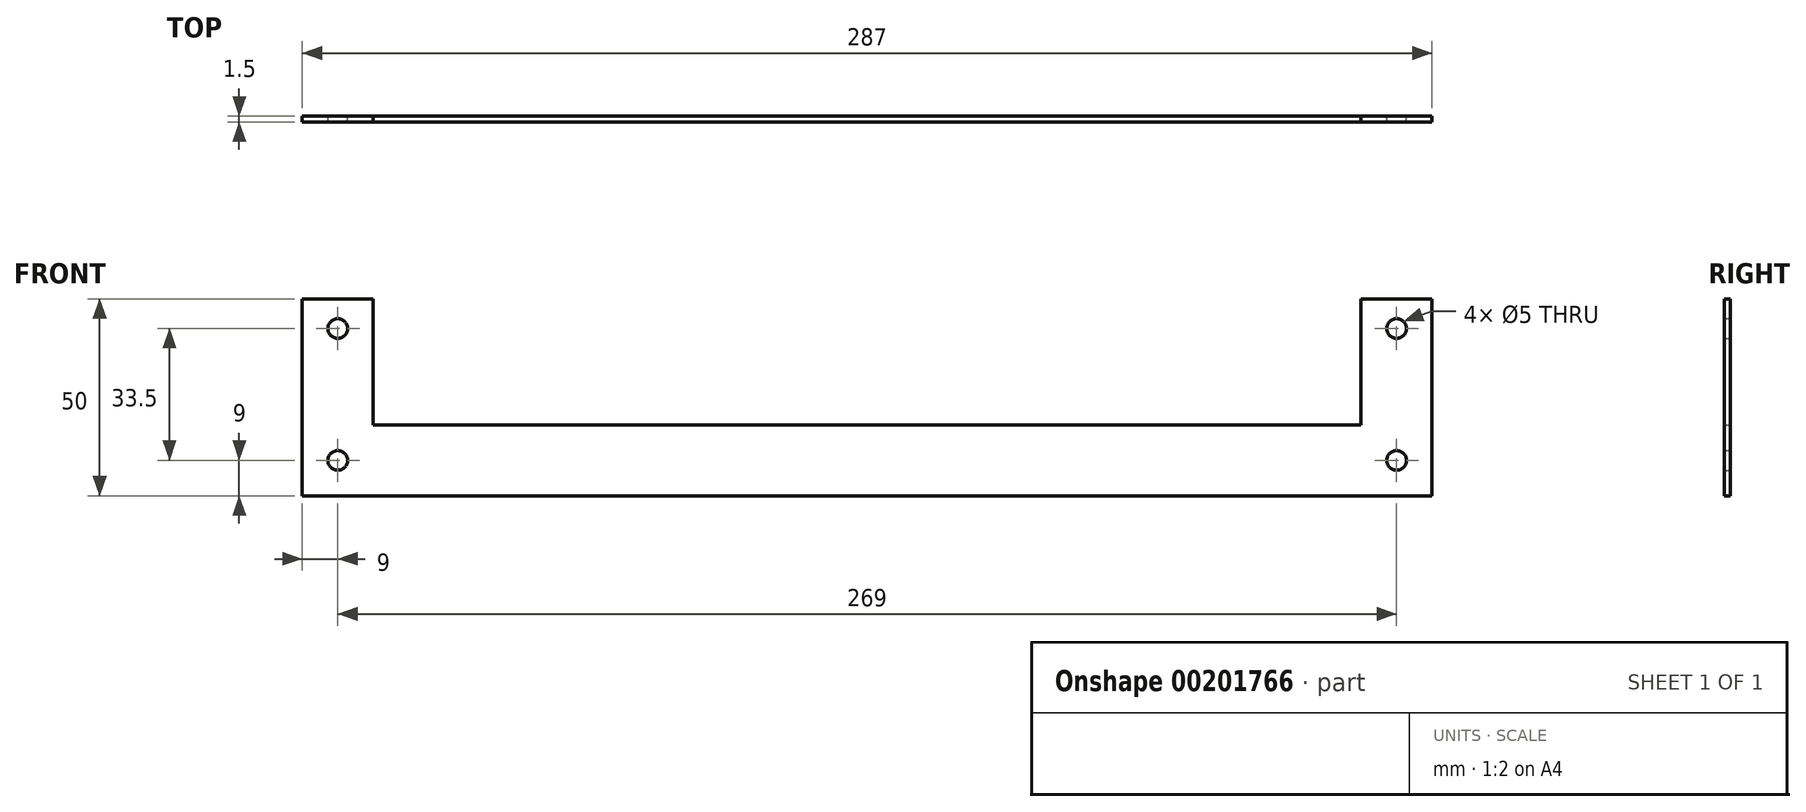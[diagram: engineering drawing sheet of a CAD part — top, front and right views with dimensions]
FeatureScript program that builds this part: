
annotation { "Feature Type Name" : "Feature", "Feature Type Description" : "" }
export const myFeature = defineFeature(function(context is Context, id is Id, definition is map)
    precondition{}
    {
        {
            var Q0;
            Q0=qCreatedBy(makeId("Front.planeOp"),FACE);
            var sketch = newSketch(context, id + "F0", { "sketchPlane" : qUnion([Q0])});
            skLineSegment(sketch, "E0", {"start": v(0, 0) * mm, "end": v(-143.5, 0) * mm});
            skLineSegment(sketch, "E1", {"start": v(-143.5, 0) * mm, "end": v(-143.5, 50) * mm});
            skLineSegment(sketch, "E2", {"start": v(-143.5, 50) * mm, "end": v(-125.5, 50) * mm});
            skLineSegment(sketch, "E3", {"start": v(-125.5, 50) * mm, "end": v(-125.5, 18) * mm});
            skLineSegment(sketch, "E4", {"start": v(-125.5, 18) * mm, "end": v(0, 18) * mm});
            skLineSegment(sketch, "E5", {"start": v(-134.5, 50) * mm, "end": v(-134.5, 0) * mm, "construction": true});
            skCircle(sketch, "E6", {"center": v(-134.5, 42.5) * mm, "radius": 2.5 * mm});
            skCircle(sketch, "E7", {"center": v(-134.5, 9) * mm, "radius": 2.5 * mm});
            skLineSegment(sketch, "E8", {"start": v(0, 0) * mm, "end": v(0, 31.13) * mm, "construction": true});
            skCircle(sketch, "E9.MirrorC", {"center": v(134.5, 42.5) * mm, "radius": 2.5 * mm});
            skCircle(sketch, "E10.MirrorC", {"center": v(134.5, 9) * mm, "radius": 2.5 * mm});
            skLineSegment(sketch, "E11.MirrorCS", {"start": v(125.5, 18) * mm, "end": v(0, 18) * mm});
            skLineSegment(sketch, "E12.MirrorCS", {"start": v(125.5, 50) * mm, "end": v(125.5, 18) * mm});
            skLineSegment(sketch, "E13.MirrorCS", {"start": v(134.5, 50) * mm, "end": v(134.5, 0) * mm, "construction": true});
            skLineSegment(sketch, "E14.MirrorCS", {"start": v(143.5, 0) * mm, "end": v(143.5, 50) * mm});
            skLineSegment(sketch, "E15.MirrorCS", {"start": v(143.5, 50) * mm, "end": v(125.5, 50) * mm});
            skLineSegment(sketch, "E16.MirrorCS", {"start": v(0, 0) * mm, "end": v(143.5, 0) * mm});
            skSolve(sketch);
        }
        {
            var Q0;
            Q0=makeQuery(id+"F0.imprint","IMPRINT",FACE,{"disambiguationData":[TD([[makeQuery(id+"F0.imprint","IMPRINT",EDGE,{"derivedFrom":sQuery(id+"F0.wireOp",EDGE,"E0")}),-1.0]])]});
            extrude(context, id + "F1", {"entities" : qUnion([Q0]), "depth" : 1.5 * mm, "offsetDistance" : 25 * mm});
        }
    });
